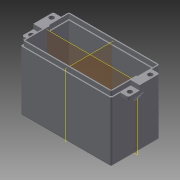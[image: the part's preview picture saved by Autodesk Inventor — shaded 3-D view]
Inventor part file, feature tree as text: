
AUTODESK INVENTOR PART (.ipt)
format: ipt  version: 2015 (Build 190159000, 159)  size: 307,200 bytes
history: native  units: mm
features: sketch x14, extrude x11, mirror x5, fillet x5, plane x3, rib x2
ambient origin geometry x8: Origin, YZ Plane, XZ Plane, XY Plane, X Axis, Y Axis, Z Axis, Center Point
bodies: Solid1 (feature_tree)
feature tree (40):
  extrude  "Extrusion1"  Depth=55.0mm
  extrude  "Extrusion2"  Depth=58.0mm
  extrude  "Extrusion3"  Depth=1.5mm
  sketch  "Sketch7"  dims[d9=55.0mm d11=58.0mm d12=1.5mm d14=1.5mm d15=0.0mm d16=28.0mm d17=0.0mm]
  plane  "Work Plane1"
  extrude  "Extrusion4"  Depth=28.0mm TaperAngle=0.0deg
  mirror  "Mirror1"
  extrude  "Extrusion5"  Depth=15.0mm
  extrude  "Extrusion6"  Depth=1.0mm
  extrude  "Extrusion7"  Depth=1.0mm TaperAngle=0.0deg
  fillet  "Fillet1"  Radius=0.75mm
  extrude  "Extrusion8"  Depth=17.0mm
  fillet  "Fillet2"  Radius=3.0mm
  fillet  "Fillet3"  Radius=0.75mm
  extrude  "Extrusion10"  Depth=3.0mm TaperAngle=0.0deg
  mirror  "Mirror3"
  fillet  "Fillet7"  Radius=4.5mm
  fillet  "Fillet8"  Radius=14.0mm
  extrude  "Extrusion11"  Depth=3.3mm
  extrude  "Extrusion12"  Depth=1.0mm
  mirror  "Mirror4"
  plane  "Work Plane5"
  rib  "Rib1"
  mirror  "Mirror5"
  plane  "Work Plane7"
  sketch  "Sketch20"  dims[d48=7.5mm]
  rib  "Rib3"
  mirror  "Mirror7"
  sketch  "Sketch3"  dims[d0=35.25mm d1=55.0mm]
  sketch  "Sketch5"  dims[d4=38.25mm d5=58.0mm]
  sketch  "Sketch6"  dims[d6=1.5mm d7=1.5mm]
  sketch  "Sketch8"  dims[d18=1.5mm d19=0.0mm d20=15.0mm]
  sketch  "Sketch9"  dims[d21=1.0mm d22=13.375mm]
  sketch  "Sketch10"  dims[d23=8.375mm d24=27.5mm d25=1.0mm d26=0.0mm d27=0.75mm]
  sketch  "Sketch11"  dims[d29=56.5mm d31=17.0mm d32=3.0mm d33=0.0mm d34=0.75mm]
  sketch  "Sketch15"  dims[d36=56.5mm d38=3.0mm d39=0.0mm d40=4.5mm d41=14.0mm]
  sketch  "Sketch16"  dims[d42=20.5mm d43=3.3mm]
  sketch  "Sketch17"  dims[d44=5.0mm d45=0.0mm d46=1.0mm]
  sketch  "Sketch18"  dims[d47=9.9mm]
  sketch  "Sketch21"  dims[d49=27.5mm d50=5.0mm d51=0.0mm d52=1.0mm d53=1.0mm d65=0.75mm d66=17.0mm d69=16.75mm d70=16.75mm d78=5.0mm d79=12.75mm d80=2.0mm d81=7.25mm d82=5.0mm d83=0.0mm d84=17.0mm d85=1.0mm d86=1.0mm d87=3.0mm d88=2.5mm d89=3.5mm d90=5.0mm d91=0.0mm d92=3.0mm d93=3.5mm d94=2.5mm d95=2.0mm d96=0.0mm d97=28.75mm d98=11.5mm d99=20.0mm d100=12.75mm d101=5.0mm d102=14.0mm d104=21.816616mm d105=1.0mm d106=2.0mm d107=0.0mm d108=0.0mm d109=1.0mm d110=1.0mm d119=-0.5mm d120=135.0deg d121=1.0mm d122=1.0mm d123=0.0mm d124=0.0mm d125=1.0mm d126=1.0mm d64=1.0mm]
